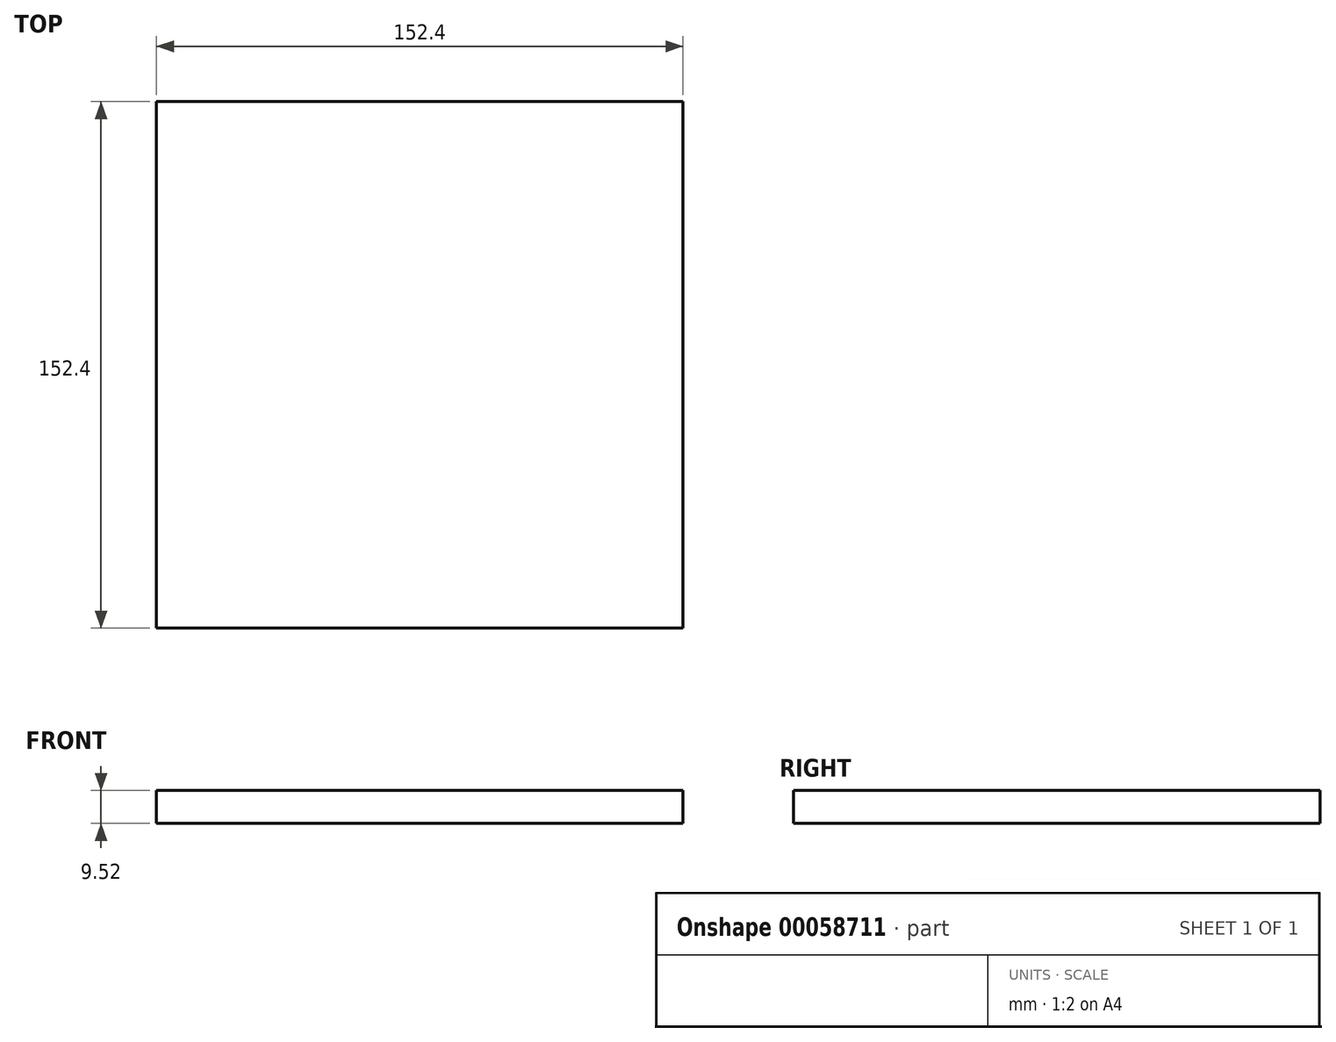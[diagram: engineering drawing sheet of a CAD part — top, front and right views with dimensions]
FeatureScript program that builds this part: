
annotation { "Feature Type Name" : "Feature", "Feature Type Description" : "" }
export const myFeature = defineFeature(function(context is Context, id is Id, definition is map)
    precondition{}
    {
        {
            var Q0;
            Q0=qCreatedBy(makeId("Top.planeOp"),FACE);
            var sketch = newSketch(context, id + "F0", { "sketchPlane" : qUnion([Q0])});
            skLineSegment(sketch, "E0.rect.bottom", {"start": v(76.2, 76.2) * mm, "end": v(-76.2, 76.2) * mm});
            skLineSegment(sketch, "E0.rect.top", {"start": v(76.2, -76.2) * mm, "end": v(-76.2, -76.2) * mm});
            skLineSegment(sketch, "E0.rect.left", {"start": v(76.2, 76.2) * mm, "end": v(76.2, -76.2) * mm});
            skLineSegment(sketch, "E0.rect.right", {"start": v(-76.2, 76.2) * mm, "end": v(-76.2, -76.2) * mm});
            skPoint(sketch, "E0.rect.middle", {"position": v(0, 0) * mm});
            skSolve(sketch);
        }
        {
            var Q0;
            Q0 = qSketchRegion(id + "F0", true);
            extrude(context, id + "F1", {"entities" : qUnion([Q0]), "endBound" : BoundingType.SYMMETRIC, "depth" : 9.52 * mm});
        }
    });
